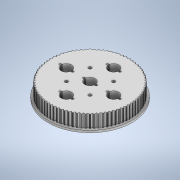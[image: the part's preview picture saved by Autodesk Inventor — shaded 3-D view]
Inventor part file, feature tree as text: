
AUTODESK INVENTOR PART (.ipt)
format: ipt  version: 2020.3 (Build 243373000, 373)  size: 1,075,200 bytes
history: native  units: mm
features: sketch x4, extrude x3, hole x1, fillet x1
ambient origin geometry x8: Origin, YZ Plane, XZ Plane, XY Plane, X Axis, Y Axis, Z Axis, Center Point
bodies: Solid1 (feature_tree)
feature tree (9):
  extrude  "Extrusion1"  Depth=2.0mm TaperAngle=0.0deg
  extrude  "Extrusion2"  Depth=76.0mm TaperAngle=360.0deg
  extrude  "Extrusion3"  Depth=10.0mm
  hole  "Hole1"  [1 undecoded]
  fillet  "Fillet1"  Radius=10.0mm
  sketch  "Sketch1"  dims[d0=80.0mm d1=2.0mm d2=0.0mm]
  sketch  "Sketch2"  dims[d3=76.0mm d4=800.0mm d6=360.0deg]
  sketch  "Sketch3"  dims[d8=12.0mm d9=0.0mm d10=10.0mm]
  sketch  "Sketch4"  dims[d11=45.0mm d13=10.0mm d14=10.0mm d15=10.0mm d16=0.0mm d17=0.0mm d18=20.0mm d19=40.0mm d21=360.0deg d23=3.0mm d25=40.0mm d26=3.0mm d28=40.0mm d29=3.0mm d31=40.0mm d32=3.0mm d33=3.0mm d34=6.0mm d35=5.6mm d36=3.2mm d37=90.0deg d38=8.0mm d39=20.594885mm d41=1.0mm d43=2.0mm d44=2.0mm d45=2.0mm d46=2.0mm d47=2.0mm d48=1.0mm]
note: 1 required parameter value undecoded (feature->parameter linkage not recoverable at this tier; creation-order binding heuristic only, values carry confidence <= 0.55)
